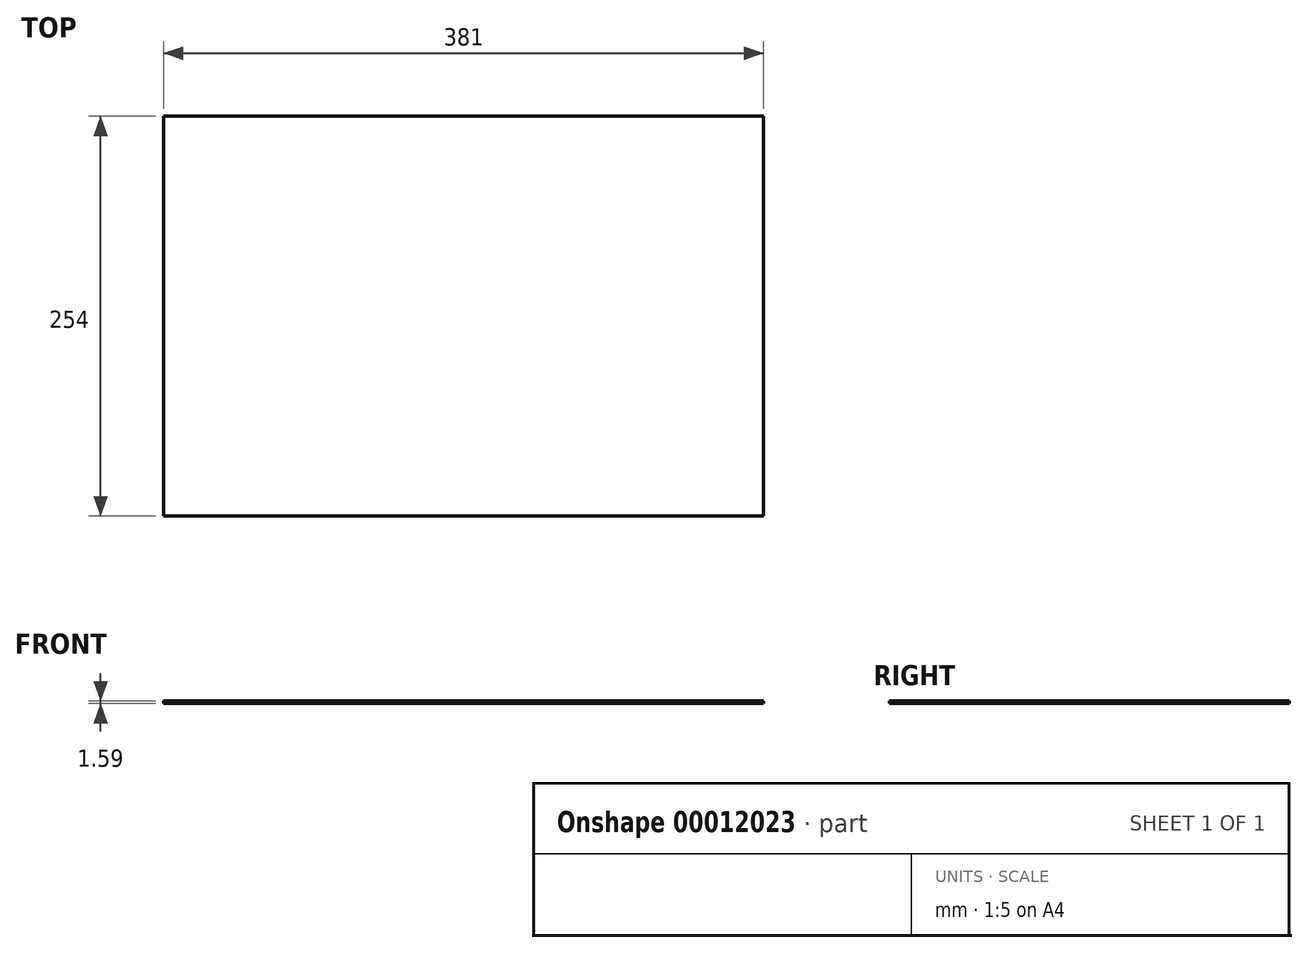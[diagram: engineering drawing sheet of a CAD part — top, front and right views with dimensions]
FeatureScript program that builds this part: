
annotation { "Feature Type Name" : "Feature", "Feature Type Description" : "" }
export const myFeature = defineFeature(function(context is Context, id is Id, definition is map)
    precondition{}
    {
        {
            var Q0;
            Q0=qCreatedBy(makeId("Top.planeOp"),FACE);
            var sketch = newSketch(context, id + "F0", { "sketchPlane" : qUnion([Q0])});
            skLineSegment(sketch, "E0.rect.bottom", {"start": v(190.5, 127) * mm, "end": v(-190.5, 127) * mm});
            skLineSegment(sketch, "E0.rect.top", {"start": v(190.5, -127) * mm, "end": v(-190.5, -127) * mm});
            skLineSegment(sketch, "E0.rect.left", {"start": v(190.5, 127) * mm, "end": v(190.5, -127) * mm});
            skLineSegment(sketch, "E0.rect.right", {"start": v(-190.5, 127) * mm, "end": v(-190.5, -127) * mm});
            skPoint(sketch, "E0.rect.middle", {"position": v(0, 0) * mm});
            skSolve(sketch);
        }
        {
            var Q0;
            Q0=makeQuery(id+"F0.imprint","IMPRINT",FACE,{"disambiguationData":[TD([[makeQuery(id+"F0.imprint","IMPRINT",EDGE,{"derivedFrom":sQuery(id+"F0.wireOp",EDGE,"E0.rect.bottom")}),1.0]])]});
            extrude(context, id + "F1", {"entities" : qUnion([Q0]), "depth" : 1.59 * mm});
        }
    });
